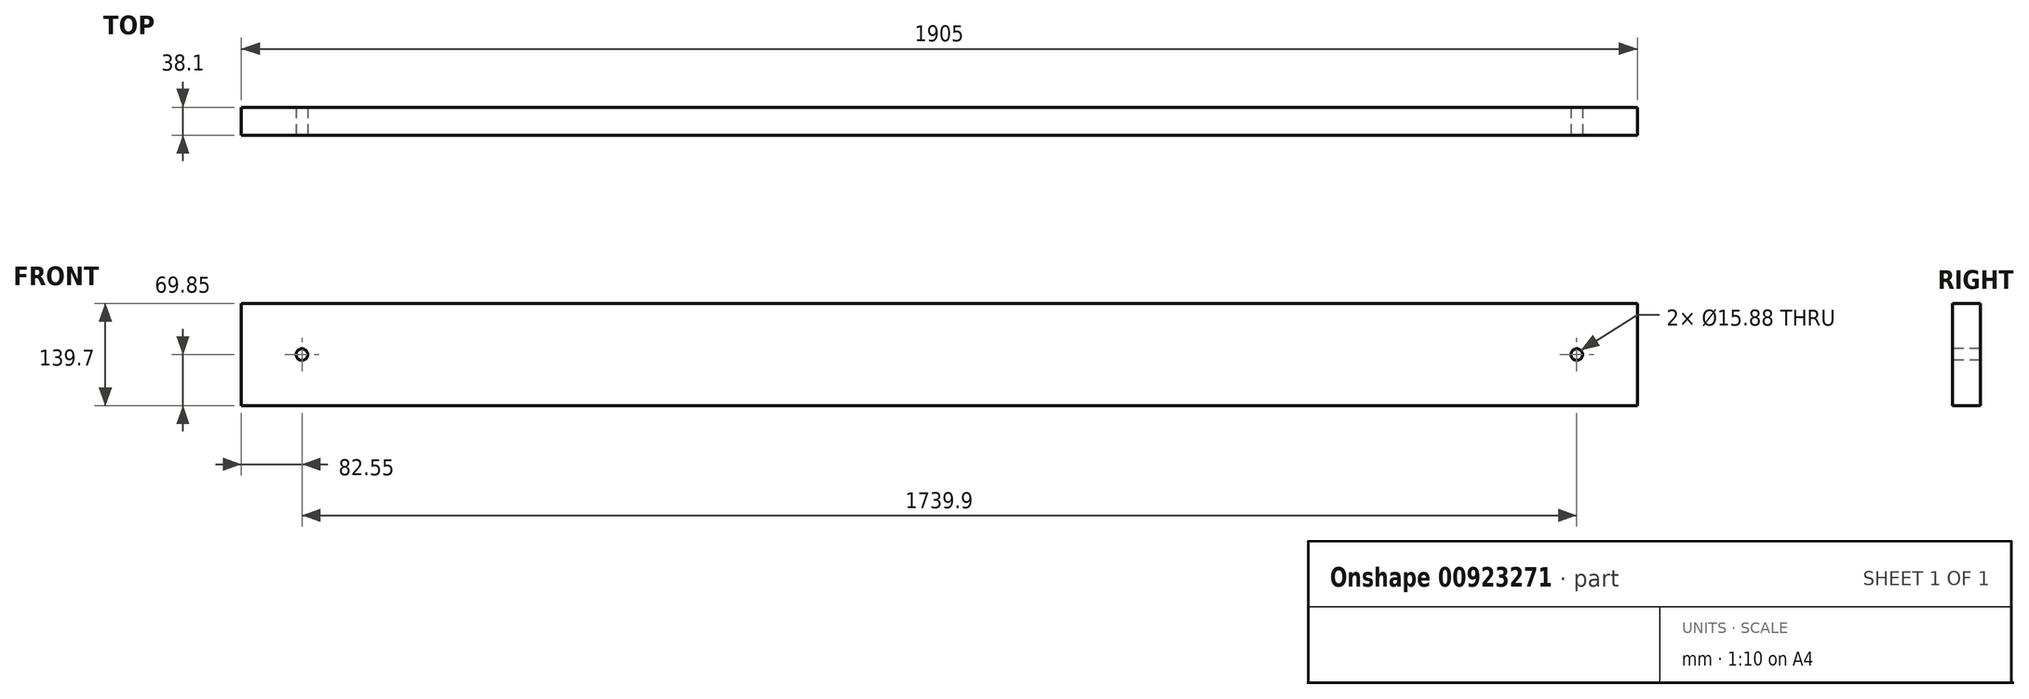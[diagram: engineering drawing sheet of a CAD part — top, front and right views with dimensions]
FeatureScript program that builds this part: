
annotation { "Feature Type Name" : "Feature", "Feature Type Description" : "" }
export const myFeature = defineFeature(function(context is Context, id is Id, definition is map)
    precondition{}
    {
        {
            var Q0;
            Q0=qCreatedBy(makeId("Top.planeOp"),FACE);
            var sketch = newSketch(context, id + "F0", { "sketchPlane" : qUnion([Q0])});
            skLineSegment(sketch, "E0.bottom", {"start": v(0, 38.1) * mm, "end": v(139.7, 38.1) * mm});
            skLineSegment(sketch, "E0.top", {"start": v(0, 0) * mm, "end": v(139.7, 0) * mm});
            skLineSegment(sketch, "E0.left", {"start": v(0, 38.1) * mm, "end": v(0, 0) * mm});
            skLineSegment(sketch, "E0.right", {"start": v(139.7, 38.1) * mm, "end": v(139.7, 0) * mm});
            skSolve(sketch);
        }
        {
            var Q0;
            Q0 = qSketchRegion(id + "F0", true);
            extrude(context, id + "F1", {"entities" : qUnion([Q0]), "depth" : 1905 * mm, "offsetDistance" : 25.4 * mm});
        }
        {
            var Q0;
            Q0=makeQuery(id+"F1.opExtrude","SWEPT_BODY",BODY,{"disambiguationData":[OSD([sQuery(id+"F0.wireOp",EDGE,"E0.bottom"),sQuery(id+"F0.wireOp",EDGE,"E0.top"),sQuery(id+"F0.wireOp",EDGE,"E0.left"),sQuery(id+"F0.wireOp",EDGE,"E0.right")])]});
            var Q1;
            Q1=makeQuery(id+"F1.opExtrude","CAP_EDGE",EDGE,{"disambiguationData":[OSD([sQuery(id+"F0.wireOp",EDGE,"E0.left")])],"isStart":true});
            transform(context, id + "F2", {"entities" : qUnion([Q0]), "transformType" : TransformType.ROTATION, "transformAxis" : qUnion([Q1]), "angle" : 90 * degree, "makeCopy" : false});
        }
        {
            var Q0;
            Q0=qCreatedBy(makeId("Front.planeOp"),FACE);
            var sketch = newSketch(context, id + "F3", { "sketchPlane" : qUnion([Q0])});
            skPoint(sketch, "E1", {"position": v(0, 69.85) * mm});
            skPoint(sketch, "E2", {"position": v(-82.55, 69.85) * mm});
            skPoint(sketch, "E3", {"position": v(-1905, 0) * mm});
            skPoint(sketch, "E4", {"position": v(-1905, 69.85) * mm});
            skPoint(sketch, "E5", {"position": v(-1822.45, 69.85) * mm});
            skSolve(sketch);
        }
        {
            var Q0;
            Q0=sQuery(id+"F3.wireOp",VERTEX,"E2");
            var Q1;
            Q1=sQuery(id+"F3.wireOp",VERTEX,"E5");
            var Q2;
            Q2=makeQuery(id+"F1.opExtrude","SWEPT_BODY",BODY,{"disambiguationData":[OSD([sQuery(id+"F0.wireOp",EDGE,"E0.bottom"),sQuery(id+"F0.wireOp",EDGE,"E0.top"),sQuery(id+"F0.wireOp",EDGE,"E0.left"),sQuery(id+"F0.wireOp",EDGE,"E0.right")])]});
            hole(context, id + "F4", {"style" : HoleStyle.SIMPLE, "endStyle" : HoleEndStyle.THROUGH, "holeDiameter" : 15.88 * mm, "majorDiameter" : 6.35 * mm, "isTappedThrough" : true, "tappedDepth" : 12.7 * mm, "tapClearance" : 3, "locations" : qUnion([Q0, Q1]), "scope" : qUnion([Q2])});
        }
    });
